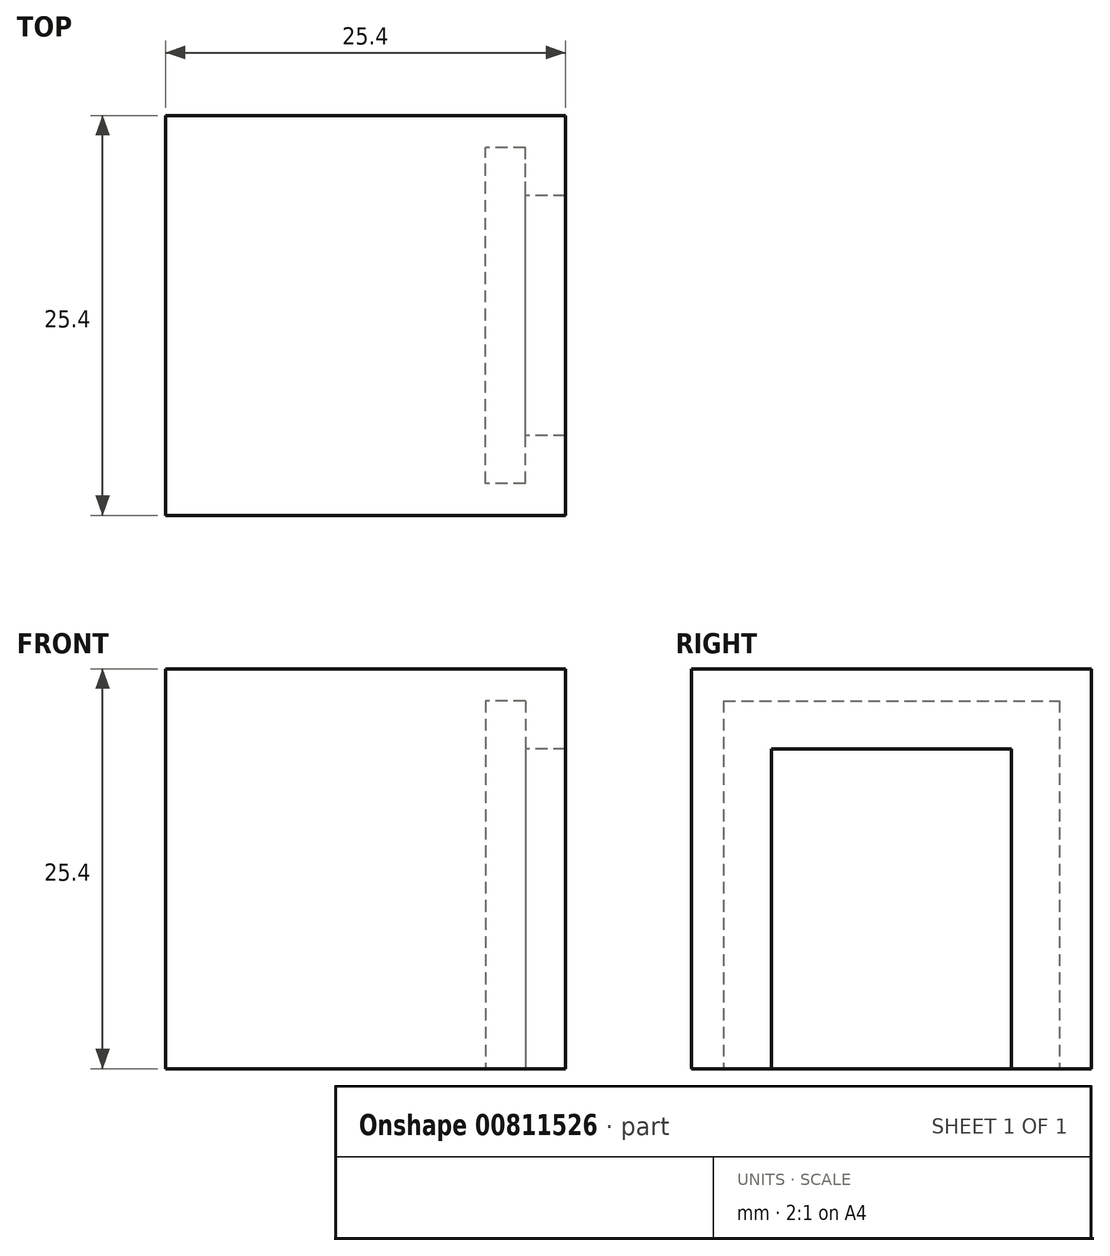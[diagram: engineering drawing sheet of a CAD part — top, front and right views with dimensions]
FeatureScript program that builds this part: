
annotation { "Feature Type Name" : "Feature", "Feature Type Description" : "" }
export const myFeature = defineFeature(function(context is Context, id is Id, definition is map)
    precondition{}
    {
        {
            var Q0;
            Q0=qCreatedBy(makeId("Top.planeOp"),FACE);
            var sketch = newSketch(context, id + "F0", { "sketchPlane" : qUnion([Q0])});
            skLineSegment(sketch, "E0.bottom", {"start": v(12.7, -12.7) * mm, "end": v(-12.7, -12.7) * mm});
            skLineSegment(sketch, "E0.top", {"start": v(12.7, 12.7) * mm, "end": v(-12.7, 12.7) * mm});
            skLineSegment(sketch, "E0.left", {"start": v(12.7, -12.7) * mm, "end": v(12.7, 12.7) * mm});
            skLineSegment(sketch, "E0.right", {"start": v(-12.7, -12.7) * mm, "end": v(-12.7, 12.7) * mm});
            skPoint(sketch, "E0.middle", {"position": v(0, 0) * mm});
            skSolve(sketch);
        }
        {
            var Q0;
            Q0=makeQuery(id+"F0.imprint","IMPRINT",FACE,{"disambiguationData":[TD([[makeQuery(id+"F0.imprint","IMPRINT",EDGE,{"derivedFrom":sQuery(id+"F0.wireOp",EDGE,"E0.bottom")}),-1.0]])]});
            extrude(context, id + "F1", {"entities" : qUnion([Q0]), "depth" : 25.4 * mm, "offsetDistance" : 25.4 * mm});
        }
        {
            var Q0;
            Q0=makeQuery(id+"F1.opExtrude","CAP_FACE",FACE,{"disambiguationData":[OSD([sQuery(id+"F0.wireOp",EDGE,"E0.bottom"),sQuery(id+"F0.wireOp",EDGE,"E0.top"),sQuery(id+"F0.wireOp",EDGE,"E0.left"),sQuery(id+"F0.wireOp",EDGE,"E0.right")])],"isStart":true});
            var sketch = newSketch(context, id + "F2", { "sketchPlane" : qUnion([Q0])});
            skLineSegment(sketch, "E1", {"start": v(12.7, 12.7) * mm, "end": v(12.7, 7.62) * mm});
            skLineSegment(sketch, "E2.bottom", {"start": v(12.7, 7.62) * mm, "end": v(10.16, 7.62) * mm});
            skLineSegment(sketch, "E2.top", {"start": v(12.7, -7.62) * mm, "end": v(10.16, -7.62) * mm});
            skLineSegment(sketch, "E2.left", {"start": v(12.7, 7.62) * mm, "end": v(12.7, -7.62) * mm});
            skLineSegment(sketch, "E2.right", {"start": v(10.16, 7.62) * mm, "end": v(10.16, -7.62) * mm});
            skLineSegment(sketch, "E3.bottom", {"start": v(10.16, 10.67) * mm, "end": v(7.62, 10.67) * mm});
            skLineSegment(sketch, "E3.top", {"start": v(10.16, -10.67) * mm, "end": v(7.62, -10.67) * mm});
            skLineSegment(sketch, "E3.left", {"start": v(10.16, 10.67) * mm, "end": v(10.16, -10.67) * mm});
            skLineSegment(sketch, "E3.right", {"start": v(7.62, 10.67) * mm, "end": v(7.62, -10.67) * mm});
            skPoint(sketch, "E3.middle", {"position": v(8.89, 0) * mm});
            skSolve(sketch);
        }
        {
            var Q0;
            {var subQ3=sQuery(id+"F2.wireOp",EDGE,"E3.bottom");Q0=makeQuery(id+"F2.imprint","IMPRINT",FACE,{"disambiguationData":[TD([[makeQuery(id+"F2.imprint","IMPRINT",EDGE,{"derivedFrom":subQ3}),1.0]])]});}
            extrude(context, id + "F3", {"entities" : qUnion([Q0]), "operationType" : NewBodyOperationType.REMOVE, "oppositeDirection" : true, "depth" : 23.37 * mm, "offsetDistance" : 25.4 * mm});
        }
        {
            var Q0;
            {var subQ0=sQuery(id+"F2.wireOp",EDGE,"E2.bottom");Q0=makeQuery(id+"F2.imprint","IMPRINT",FACE,{"disambiguationData":[TD([[makeQuery(id+"F2.imprint","IMPRINT",EDGE,{"derivedFrom":subQ0}),1.0]])]});}
            extrude(context, id + "F4", {"entities" : qUnion([Q0]), "operationType" : NewBodyOperationType.REMOVE, "oppositeDirection" : true, "depth" : 20.32 * mm, "offsetDistance" : 25.4 * mm});
        }
    });
